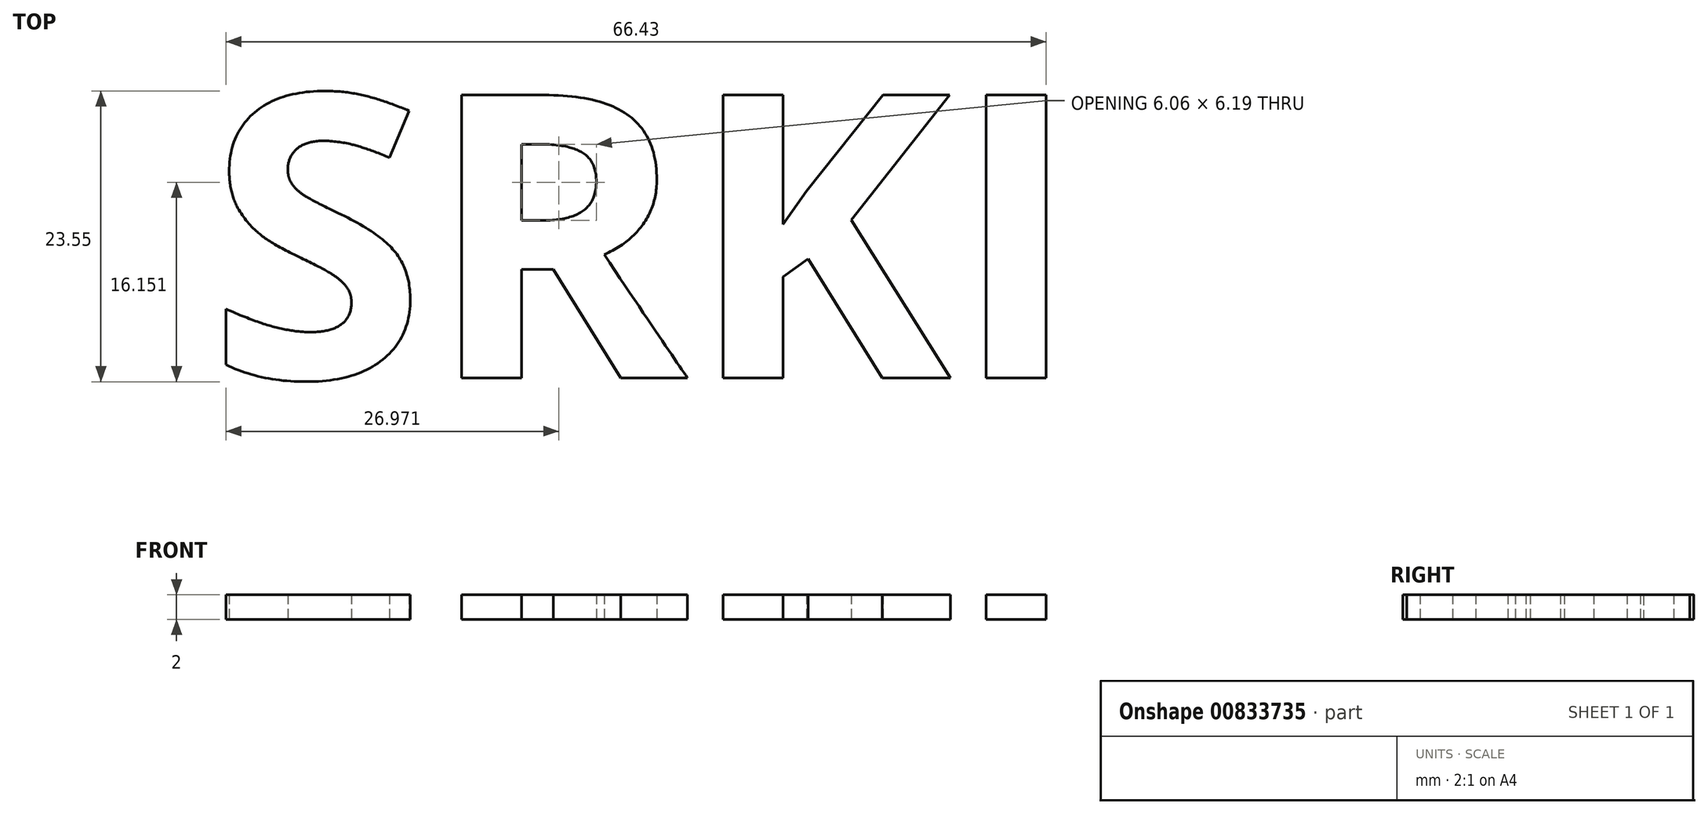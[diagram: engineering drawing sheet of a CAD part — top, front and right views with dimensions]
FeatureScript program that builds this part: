
annotation { "Feature Type Name" : "Feature", "Feature Type Description" : "" }
export const myFeature = defineFeature(function(context is Context, id is Id, definition is map)
    precondition{}
    {
        {
            var Q0;
            Q0=qCreatedBy(makeId("Top.planeOp"),FACE);
            var sketch = newSketch(context, id + "F0", { "sketchPlane" : qUnion([Q0])});
            skText(sketch, "E0", { "text": "SRKI", "fontName": "OpenSans-Bold.ttf"});
            const initialGuessF0  = {"E0": [-0.03487, -0.00985, 1, 0, 0.0231]};
            skSetInitialGuess(sketch, initialGuessF0);
            skSolve(sketch);
        }
        {
            var Q0;
            Q0 = qSketchRegion(id + "F0", true);
            extrude(context, id + "F1", {"entities" : qUnion([Q0]), "depth" : 2 * mm, "offsetDistance" : 25 * mm});
        }
    });
